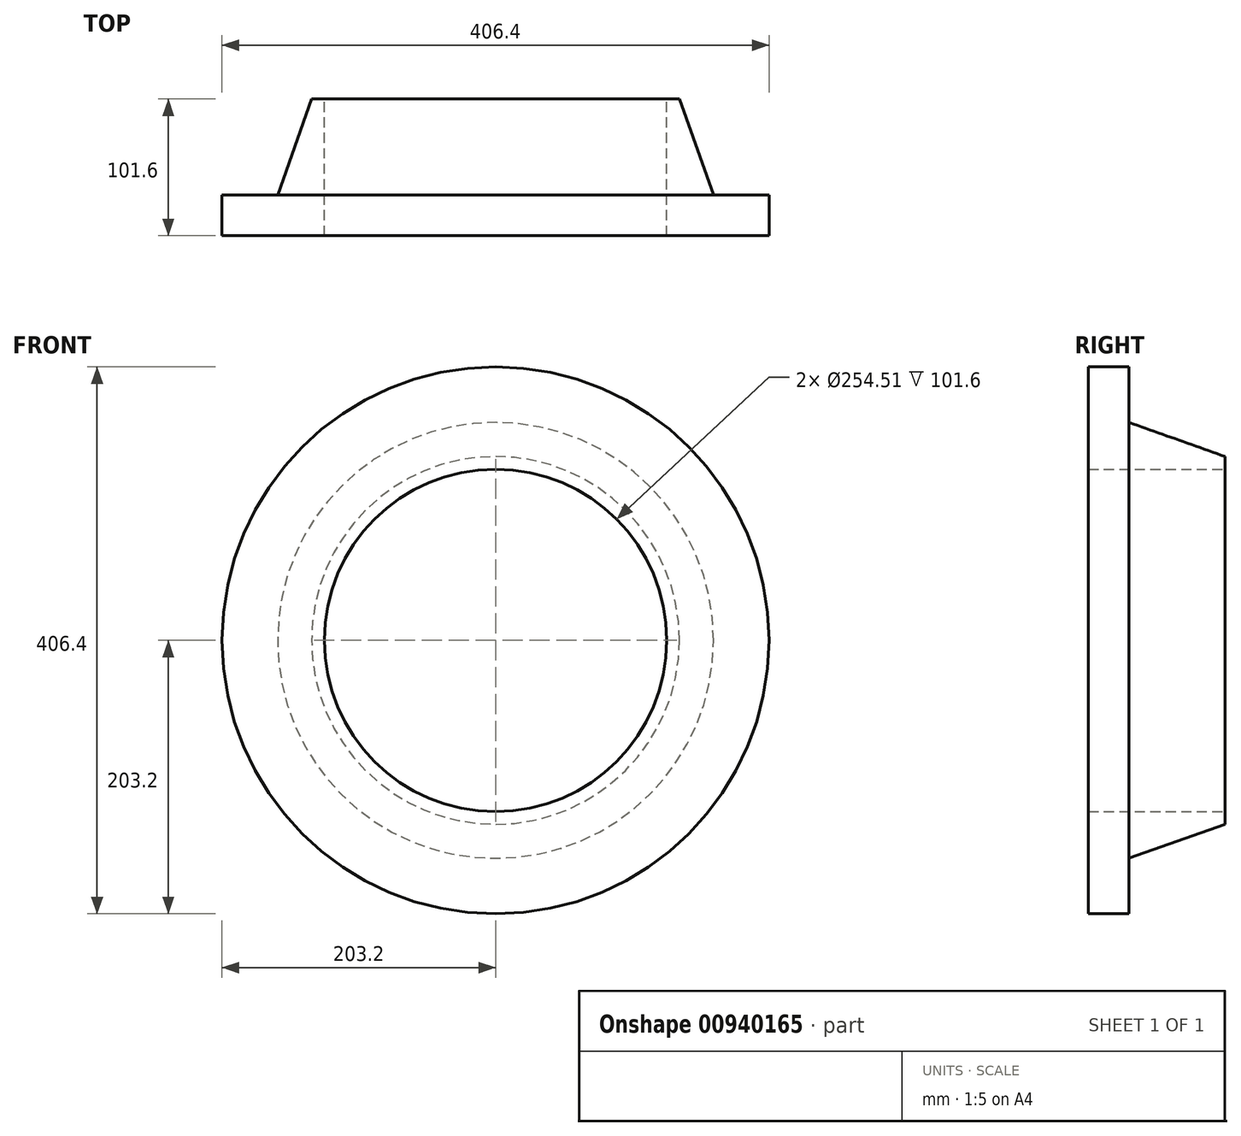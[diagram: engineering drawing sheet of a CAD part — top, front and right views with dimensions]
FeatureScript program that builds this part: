
annotation { "Feature Type Name" : "Feature", "Feature Type Description" : "" }
export const myFeature = defineFeature(function(context is Context, id is Id, definition is map)
    precondition{}
    {
        {
            var Q0;
            Q0=qCreatedBy(makeId("Top.planeOp"),FACE);
            var sketch = newSketch(context, id + "F0", { "sketchPlane" : qUnion([Q0])});
            skLineSegment(sketch, "E0", {"start": v(0, 0) * mm, "end": v(203.2, 0) * mm, "construction": true});
            skLineSegment(sketch, "E1", {"start": v(203.2, 0) * mm, "end": v(203.2, 30.16) * mm});
            skLineSegment(sketch, "E2", {"start": v(203.2, 30.16) * mm, "end": v(161.92, 30.16) * mm});
            skLineSegment(sketch, "E3", {"start": v(161.92, 30.16) * mm, "end": v(136.65, 101.6) * mm});
            skLineSegment(sketch, "E4", {"start": v(136.65, 101.6) * mm, "end": v(127.25, 101.6) * mm});
            skLineSegment(sketch, "E5", {"start": v(127.25, 101.6) * mm, "end": v(127.25, 0) * mm});
            skLineSegment(sketch, "E6", {"start": v(127.25, 0) * mm, "end": v(203.2, 0) * mm});
            skLineSegment(sketch, "E7", {"start": v(0, 101.6) * mm, "end": v(0, 0) * mm, "construction": true});
            skSolve(sketch);
        }
        {
            var Q0;
            Q0=qSketchRegion(id+"F0",true);
            var Q1;
            Q1=sQuery(id+"F0.wireOp",EDGE,"E7");
            revolve(context, id + "F1", {"entities" : qUnion([Q0]), "axis" : qUnion([Q1]), "revolveType" : RevolveType.FULL});
        }
    });
